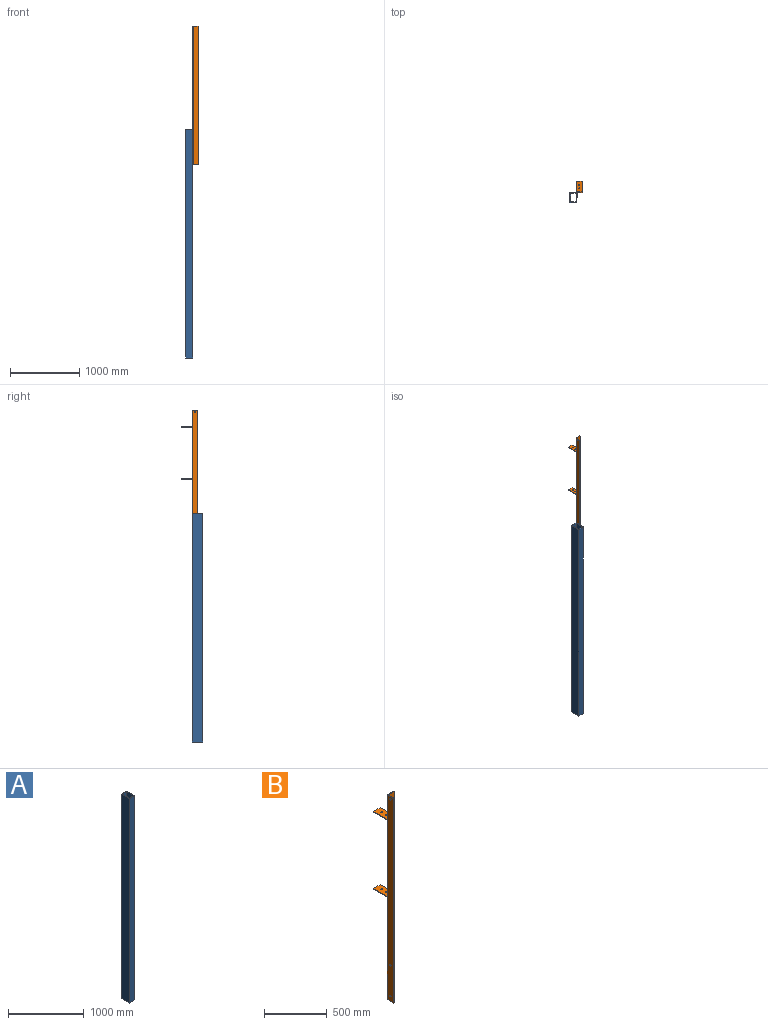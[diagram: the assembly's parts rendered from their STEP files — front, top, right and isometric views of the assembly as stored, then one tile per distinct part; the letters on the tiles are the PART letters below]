
ASSEMBLY  parts=2 mates=1
PART A: 10 faces, bbox 100x150x3300 mm
  f0: plane 3300x150mm, normal (-1,0,0), area 495000mm2, adj f1,f7,f8,f9
  f1: plane 3300x100mm, normal (0,-1,0), area 330000mm2, adj f0,f2,f8,f9
  f2: plane 3300x150mm, normal (1,0,0), area 495000mm2, adj f1,f7,f8,f9
  f3: plane 3300x80mm, normal (0,1,0), area 264000mm2, adj f4,f6,f8,f9
  f4: plane 3300x130mm, normal (1,0,0), area 429000mm2, adj f3,f5,f8,f9
  f5: plane 3300x80mm, normal (0,-1,0), area 264000mm2, adj f4,f6,f8,f9
  f6: plane 3300x130mm, normal (-1,0,0), area 429000mm2, adj f3,f5,f8,f9
  f7: plane 3300x100mm, normal (0,1,0), area 330000mm2, adj f0,f2,f8,f9
  f8: plane 150x100mm, normal (0,0,1), area 4600mm2, adj f0,f1,f2,f3,f4,f5,f6,f7
  f9: plane 150x100mm, normal (0,0,-1), area 4600mm2, adj f0,f1,f2,f3,f4,f5,f6,f7
PART B: 27 faces, bbox 75x230x2000 mm
  f0: plane 235x75mm, normal (0,1,0), area 17625mm2, adj f4,f6,f8,f23
  f1: plane 738x75mm, normal (0,1,0), area 55350mm2, adj f4,f6,f24,f25
  f2: plane 2000x69mm, normal (1,0,0), area 137469.9mm2, adj f3,f7,f8,f9,f10,f11,f12
  f3: plane 2000x69mm, normal (0,-1,0), area 138000mm2, adj f2,f4,f8,f9
  f4: plane 2000x161mm, normal (1,0,0), area 13881.5mm2, adj f0,f1,f3,f5,f8,f9,f13,f14
  f5: plane 995x75mm, normal (0,1,0), area 74625mm2, adj f4,f6,f9,f26
  f6: plane 2000x230mm, normal (-1,0,0), area 151351.3mm2, adj f0,f1,f5,f7,f8,f9,f10,f11
  f7: plane 2000x6mm, normal (0,-1,0), area 12000mm2, adj f2,f6,f8,f9
  f8: plane 75x75mm, normal (0,0,1), area 864mm2, adj f0,f2,f3,f4,f6,f7
  f9: plane 75x75mm, normal (0,0,-1), area 864mm2, adj f2,f3,f4,f5,f6,f7
  f10: cylinder r=7.5mm len=15mm, axis (-1,0,0), area 282.7mm2, adj f2,f6
  f11: cylinder r=7.5mm len=15mm, axis (-1,0,0), area 282.7mm2, adj f2,f6
  f12: cylinder r=7.5mm len=15mm, axis (-1,0,0), area 282.7mm2, adj f2,f6
  f13: plane 150x75mm, normal (0,0,1), area 10896.6mm2, adj f4,f6,f15,f21,f22,f25
  f14: plane 150x75mm, normal (0,0,-1), area 10896.6mm2, adj f4,f6,f15,f21,f22,f26
  f15: plane 75x6mm, normal (0,1,0), area 450mm2, adj f4,f6,f13,f14
  f16: plane 150x75mm, normal (0,0,1), area 10896.6mm2, adj f4,f6,f18,f19,f20,f23
  f17: plane 150x75mm, normal (0,0,-1), area 10896.6mm2, adj f4,f6,f18,f19,f20,f24
  f18: plane 75x6mm, normal (0,1,0), area 450mm2, adj f4,f6,f16,f17
  f19: cylinder r=7.5mm len=15mm, axis (0,0,-1), area 282.7mm2, adj f16,f17
  f20: cylinder r=7.5mm len=15mm, axis (0,0,-1), area 282.7mm2, adj f16,f17
  f21: cylinder r=7.5mm len=15mm, axis (0,0,-1), area 282.7mm2, adj f13,f14
  f22: cylinder r=7.5mm len=15mm, axis (0,0,-1), area 282.7mm2, adj f13,f14
  f23: cylinder r=5mm len=75mm, axis (1,0,0), area 589mm2, adj f0,f4,f6,f16
  f24: cylinder r=5mm len=75mm, axis (-1,0,0), area 589mm2, adj f1,f4,f6,f17
  f25: cylinder r=5mm len=75mm, axis (1,0,0), area 589mm2, adj f1,f4,f6,f13
  f26: cylinder r=5mm len=75mm, axis (1,0,0), area 589mm2, adj f4,f5,f6,f14
PLACE A t=(6172.2,-4281.26,-13417.17)mm fixed
PLACE B t=(6222.2,-4206.26,-10117.17)mm
MATE fastened B.f10 <-> A.f2  axis (-1,0,0) through (6222.2,-4241.26,-10267.17)mm
